# Revit family: R 10 (a)
name_source: partatom
category: Equipement spécialisé
revit_build: Autodesk Revit LT 2015 (Build: 20140606_1530(x64)
units: mm (PartAtom-declared; Revit-internal decimal feet)

## types (5) — shared parameters
Apparent Power = 0 VA
Depth = 595 mm
Description = CUTTERS DE TABLE
Electrique connexion = 110 mm
Fabricant = ROBOT COUPE
Height = 660 mm
Phase = 3
UP Depth = 720 mm
UP Height = 910 mm
URL = www.robot-coupe.com
Width = 395 mm
water = Connector
zero-valued in all types: Cold water supply, Cold water supply height, Used water, Waste water height

## per-type parameters (varying)
| type | Amps | Cycle | HP | Modèle | Speeds (Rpm) | Volts | Watts | Weight |
| R 10   230/50/3 | 6 & 10 A | 50 Hz |  | R 10 | 1500 & 3000 | 230 V | 2600 W | 49.7 kg |
| R 10   400/50/3 | 6 & 11 A | 50 Hz |  | R 10 | 1500 & 3000 | 400 V | 2600 W | 49.7 kg |
| R 10   220/60/3 | 6 & 10 A | 60 Hz |  | R 10 | 1500 & 3000 | 220 V | 2600 W | 49.7 kg |
| R 10   380/60/3 | 6.5 & 11 A | 60 Hz |  | R 10 | 1500 & 3000 | 380 V | 2600 W | 49.7 kg |
| R 10  USA   208-240/60/3 |  | 60 Hz | 4.5 | R 10 USA | 1800 & 3600 | 208 V | 0 W | 155 lbs |

## geometry (parser evidence)
native form markers: Blend x104, Sweep x5
no freeform markers — native parametric forms only
